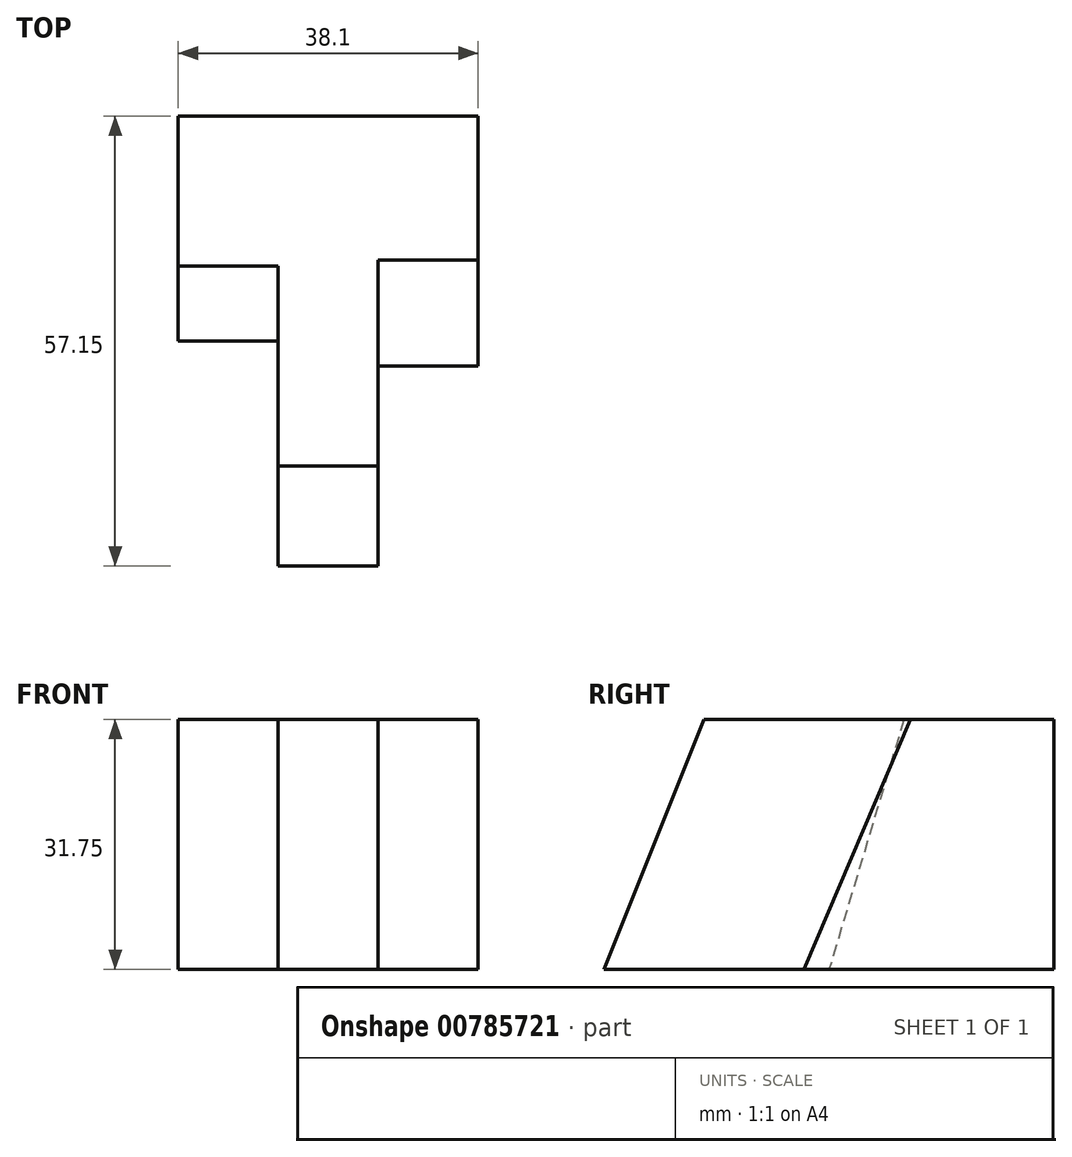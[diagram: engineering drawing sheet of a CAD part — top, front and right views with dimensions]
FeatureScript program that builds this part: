
annotation { "Feature Type Name" : "Feature", "Feature Type Description" : "" }
export const myFeature = defineFeature(function(context is Context, id is Id, definition is map)
    precondition{}
    {
        {
            var Q0;
            Q0=qCreatedBy(makeId("Front.planeOp"),FACE);
            var sketch = newSketch(context, id + "F0", { "sketchPlane" : qUnion([Q0])});
            skLineSegment(sketch, "E0", {"start": v(0, 0) * mm, "end": v(38.1, 0) * mm});
            skLineSegment(sketch, "E1", {"start": v(38.1, 0) * mm, "end": v(38.1, 31.75) * mm});
            skLineSegment(sketch, "E2", {"start": v(38.1, 31.75) * mm, "end": v(0, 31.75) * mm});
            skLineSegment(sketch, "E3", {"start": v(0, 0) * mm, "end": v(0, 31.75) * mm});
            skSolve(sketch);
        }
        {
            var Q0;
            Q0=makeQuery(id+"F0.imprint","IMPRINT",FACE,{"disambiguationData":[TD([[makeQuery(id+"F0.imprint","IMPRINT",EDGE,{"derivedFrom":sQuery(id+"F0.wireOp",EDGE,"E0")}),1.0]])]});
            extrude(context, id + "F1", {"entities" : qUnion([Q0]), "depth" : 57.15 * mm, "offsetDistance" : 25.4 * mm});
        }
        {
            var Q0;
            Q0=makeQuery(id+"F1.opExtrude","SWEPT_FACE",FACE,{"disambiguationData":[OSD([sQuery(id+"F0.wireOp",EDGE,"E3")])]});
            var sketch = newSketch(context, id + "F2", { "sketchPlane" : qUnion([Q0])});
            skLineSegment(sketch, "E4", {"start": v(0, 31.75) * mm, "end": v(19.05, 31.75) * mm});
            skLineSegment(sketch, "E5", {"start": v(0, 0) * mm, "end": v(28.58, 0) * mm});
            skLineSegment(sketch, "E6", {"start": v(19.05, 31.75) * mm, "end": v(28.58, 0) * mm});
            skSolve(sketch);
        }
        {
            var Q0;
            {var subQ0=sQuery(id+"F2.wireOp",EDGE,"E6");Q0=makeQuery(id+"F2.imprint","IMPRINT",FACE,{"disambiguationData":[TD([[makeQuery(id+"F2.imprint","IMPRINT",EDGE,{"derivedFrom":subQ0}),1.0]])]});}
            extrude(context, id + "F3", {"entities" : qUnion([Q0]), "operationType" : NewBodyOperationType.REMOVE, "oppositeDirection" : true, "depth" : 12.7 * mm, "offsetDistance" : 25.4 * mm});
        }
        {
            var Q0;
            Q0=makeQuery(id+"F1.opExtrude","SWEPT_FACE",FACE,{"disambiguationData":[OSD([sQuery(id+"F0.wireOp",EDGE,"E1")])]});
            var sketch = newSketch(context, id + "F4", { "sketchPlane" : qUnion([Q0])});
            skLineSegment(sketch, "E7", {"start": v(0, 31.75) * mm, "end": v(-18.26, 31.75) * mm});
            skLineSegment(sketch, "E8", {"start": v(0, 0) * mm, "end": v(-31.75, 0) * mm});
            skLineSegment(sketch, "E9", {"start": v(-18.26, 31.75) * mm, "end": v(-31.75, 0) * mm});
            skSolve(sketch);
        }
        {
            var Q0;
            {var subQ0=sQuery(id+"F4.wireOp",EDGE,"E9");Q0=makeQuery(id+"F4.imprint","IMPRINT",FACE,{"disambiguationData":[TD([[makeQuery(id+"F4.imprint","IMPRINT",EDGE,{"derivedFrom":subQ0}),-1.0]])]});}
            extrude(context, id + "F5", {"entities" : qUnion([Q0]), "operationType" : NewBodyOperationType.REMOVE, "oppositeDirection" : true, "depth" : 12.7 * mm, "offsetDistance" : 25.4 * mm});
        }
        {
            var Q0;
            Q0=makeQuery(id+"F3.boolean.opBoolean","COPY",FACE,{"derivedFrom":makeQuery(id+"F3.opExtrude","CAP_FACE",FACE,{"disambiguationData":[OSD([sQuery(id+"F0.wireOp",EDGE,"E0"),sQuery(id+"F0.wireOp",EDGE,"E2"),sQuery(id+"F0.wireOp",EDGE,"E3"),sQuery(id+"F2.wireOp",EDGE,"E6")])],"isStart":false})});
            var sketch = newSketch(context, id + "F6", { "sketchPlane" : qUnion([Q0])});
            skLineSegment(sketch, "E10", {"start": v(57.15, 31.75) * mm, "end": v(44.45, 31.75) * mm});
            skLineSegment(sketch, "E11", {"start": v(44.45, 31.75) * mm, "end": v(57.15, 0) * mm});
            skSolve(sketch);
        }
        {
            var Q0;
            Q0=makeQuery(id+"F6.imprint","IMPRINT",FACE,{"disambiguationData":[TD([[makeQuery(id+"F6.imprint","IMPRINT",EDGE,{"derivedFrom":sQuery(id+"F6.wireOp",EDGE,"E10")}),1.0]])]});
            extrude(context, id + "F7", {"entities" : qUnion([Q0]), "operationType" : NewBodyOperationType.REMOVE, "oppositeDirection" : true, "depth" : 25.4 * mm, "offsetDistance" : 25.4 * mm});
        }
    });
